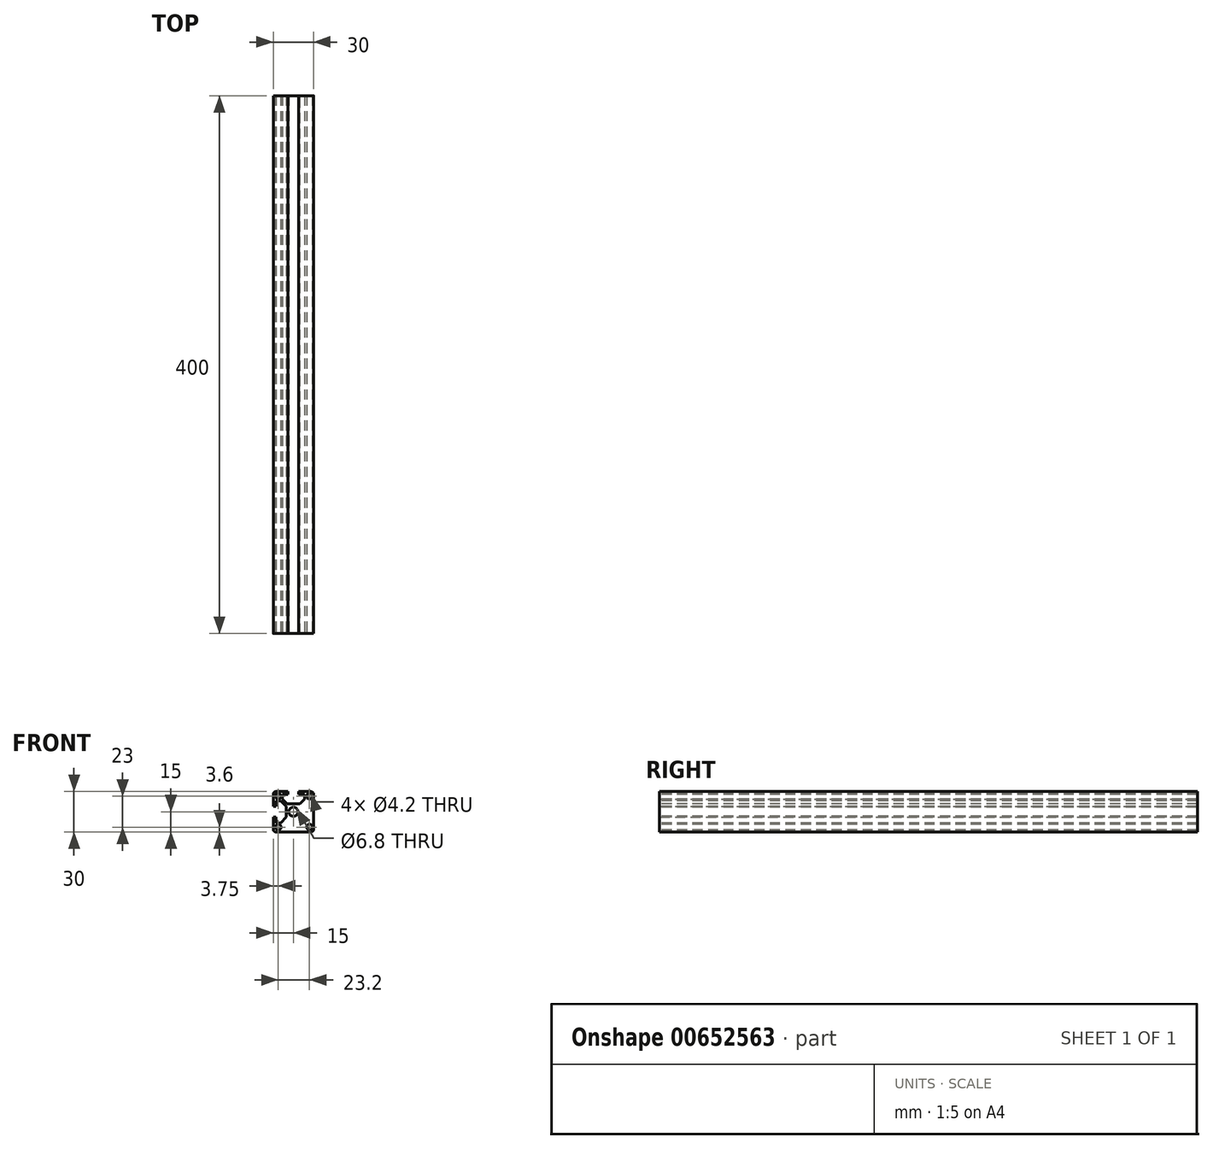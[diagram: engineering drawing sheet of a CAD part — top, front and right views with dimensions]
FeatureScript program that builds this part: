
annotation { "Feature Type Name" : "Feature", "Feature Type Description" : "" }
export const myFeature = defineFeature(function(context is Context, id is Id, definition is map)
    precondition{}
    {
        {
            var Q0;
            Q0=qCreatedBy(makeId("Front.planeOp"),FACE);
            var sketch = newSketch(context, id + "F0", { "sketchPlane" : qUnion([Q0])});
            skLineSegment(sketch, "E0.bottom", {"start": v(15, 15) * mm, "end": v(-15, 15) * mm});
            skLineSegment(sketch, "E0.top", {"start": v(15, -15) * mm, "end": v(-15, -15) * mm});
            skLineSegment(sketch, "E0.left", {"start": v(15, 15) * mm, "end": v(15, -15) * mm});
            skLineSegment(sketch, "E0.right", {"start": v(-15, 15) * mm, "end": v(-15, -15) * mm});
            skPoint(sketch, "E0.middle", {"position": v(0, 0) * mm});
            skSolve(sketch);
        }
        {
            var Q0;
            Q0=makeQuery(id+"F0.imprint","IMPRINT",FACE,{"disambiguationData":[TD([[makeQuery(id+"F0.imprint","IMPRINT",EDGE,{"derivedFrom":sQuery(id+"F0.wireOp",EDGE,"E0.bottom")}),1.0]])]});
            extrude(context, id + "F1", {"entities" : qUnion([Q0]), "depth" : 400 * mm, "offsetDistance" : 25 * mm});
        }
        {
            var Q0;
            Q0=makeQuery(id+"F1.opExtrude","CAP_FACE",FACE,{"disambiguationData":[OSD([sQuery(id+"F0.wireOp",EDGE,"E0.bottom"),sQuery(id+"F0.wireOp",EDGE,"E0.top"),sQuery(id+"F0.wireOp",EDGE,"E0.left"),sQuery(id+"F0.wireOp",EDGE,"E0.right")])],"isStart":false});
            var sketch = newSketch(context, id + "F2", { "sketchPlane" : qUnion([Q0])});
            skLineSegment(sketch, "E1.bottom", {"start": v(-4, 18.26) * mm, "end": v(4, 18.26) * mm});
            skLineSegment(sketch, "E1.top", {"start": v(-4, 13) * mm, "end": v(4, 13) * mm});
            skLineSegment(sketch, "E1.left", {"start": v(-4, 18.26) * mm, "end": v(-4, 13) * mm});
            skLineSegment(sketch, "E1.right", {"start": v(4, 18.26) * mm, "end": v(4, 13) * mm});
            skLineSegment(sketch, "E2.bottom", {"start": v(-8.25, 13) * mm, "end": v(8.25, 13) * mm});
            skLineSegment(sketch, "E2.top", {"start": v(-8.25, 6) * mm, "end": v(8.25, 6) * mm});
            skLineSegment(sketch, "E2.left", {"start": v(-8.25, 13) * mm, "end": v(-8.25, 6) * mm});
            skLineSegment(sketch, "E2.right", {"start": v(8.25, 13) * mm, "end": v(8.25, 6) * mm});
            skSolve(sketch);
        }
        {
            var Q0;
            Q0=makeQuery(id+"F2.imprint","IMPRINT",FACE,{"disambiguationData":[TD([[makeQuery(id+"F2.imprint","IMPRINT",EDGE,{"derivedFrom":sQuery(id+"F2.wireOp",EDGE,"E2.top")}),1.0]])]});
            var Q1;
            {var subQ0=sQuery(id+"F2.wireOp",EDGE,"E2.bottom");var subQ1=sQuery(id+"F2.wireOp",EDGE,"E1.left");var subQ2=makeQuery(id+"F2.imprint","INTERSECT",VERTEX,{"derivedFrom":[subQ1,subQ0]});Q1=makeQuery(id+"F2.imprint","IMPRINT",FACE,{"disambiguationData":[TD([[makeQuery(id+"F2.imprint","IMPRINT",EDGE,{"disambiguationData":[TD([[subQ2,1.0]])],"derivedFrom":subQ1}),1.0]])]});}
            var Q2;
            {var subQ0=sQuery(id+"F2.wireOp",EDGE,"E1.bottom");Q2=makeQuery(id+"F2.imprint","IMPRINT",FACE,{"disambiguationData":[TD([[makeQuery(id+"F2.imprint","IMPRINT",EDGE,{"derivedFrom":subQ0}),-1.0]])]});}
            extrude(context, id + "F3", {"entities" : qUnion([Q0, Q1, Q2]), "operationType" : NewBodyOperationType.REMOVE, "oppositeDirection" : true, "depth" : 400 * mm, "offsetDistance" : 25 * mm});
        }
        {
            var Q0;
            Q0=makeQuery(id+"F3.boolean.opBoolean","COPY",EDGE,{"derivedFrom":makeQuery(id+"F3.opExtrude","SWEPT_EDGE",EDGE,{"disambiguationData":[OSD([sQuery(id+"F2.wireOp",EDGE,"E2.top"),sQuery(id+"F2.wireOp",EDGE,"E2.left")])]})});
            var Q1;
            Q1=makeQuery(id+"F3.boolean.opBoolean","COPY",EDGE,{"derivedFrom":makeQuery(id+"F3.opExtrude","SWEPT_EDGE",EDGE,{"disambiguationData":[OSD([sQuery(id+"F2.wireOp",EDGE,"E2.top"),sQuery(id+"F2.wireOp",EDGE,"E2.right")])]})});
            chamfer(context, id + "F4", {"entities" : qUnion([Q0, Q1]), "width" : 3.5 * mm, "tangentPropagation" : true});
        }
        {
            var Q0;
            Q0=makeQuery(id+"F1.opExtrude","CAP_FACE",FACE,{"disambiguationData":[OSD([sQuery(id+"F0.wireOp",EDGE,"E0.bottom"),sQuery(id+"F0.wireOp",EDGE,"E0.top"),sQuery(id+"F0.wireOp",EDGE,"E0.left"),sQuery(id+"F0.wireOp",EDGE,"E0.right")])],"isStart":false});
            var sketch = newSketch(context, id + "F5", { "sketchPlane" : qUnion([Q0])});
            skLineSegment(sketch, "E3.bottom", {"start": v(-18.87, 4) * mm, "end": v(-13, 4) * mm});
            skLineSegment(sketch, "E3.top", {"start": v(-18.87, -4) * mm, "end": v(-13, -4) * mm});
            skLineSegment(sketch, "E3.left", {"start": v(-18.87, 4) * mm, "end": v(-18.87, -4) * mm});
            skLineSegment(sketch, "E4.bottom", {"start": v(-13, 8.25) * mm, "end": v(-9.5, 8.25) * mm});
            skLineSegment(sketch, "E4.top", {"start": v(-13, -8.25) * mm, "end": v(-9.5, -8.25) * mm});
            skLineSegment(sketch, "E4.left", {"start": v(-13, 8.25) * mm, "end": v(-13, 4) * mm});
            skLineSegment(sketch, "E4.right", {"start": v(-5.31, 4.06) * mm, "end": v(-5.31, -4.06) * mm});
            skLineSegment(sketch, "E5", {"start": v(-9.5, 8.25) * mm, "end": v(-5.31, 4.06) * mm});
            skLineSegment(sketch, "E6", {"start": v(-5.31, -4.06) * mm, "end": v(-9.5, -8.25) * mm});
            skLineSegment(sketch, "E7.trimOffspring", {"start": v(-13, -4) * mm, "end": v(-13, -8.25) * mm});
            skSolve(sketch);
        }
        {
            var Q0;
            {var subQ0=sQuery(id+"F5.wireOp",EDGE,"E3.left");Q0=makeQuery(id+"F5.imprint","IMPRINT",FACE,{"disambiguationData":[TD([[makeQuery(id+"F5.imprint","IMPRINT",EDGE,{"derivedFrom":subQ0}),1.0]])]});}
            var Q1;
            Q1=makeQuery(id+"F5.imprint","IMPRINT",FACE,{"disambiguationData":[TD([[makeQuery(id+"F5.imprint","IMPRINT",EDGE,{"derivedFrom":sQuery(id+"F5.wireOp",EDGE,"E4.bottom")}),-1.0]])]});
            extrude(context, id + "F6", {"entities" : qUnion([Q0, Q1]), "operationType" : NewBodyOperationType.REMOVE, "oppositeDirection" : true, "depth" : 400 * mm, "offsetDistance" : 25 * mm});
        }
        {
            var Q0;
            Q0=makeQuery(id+"F1.opExtrude","CAP_FACE",FACE,{"disambiguationData":[OSD([sQuery(id+"F0.wireOp",EDGE,"E0.bottom"),sQuery(id+"F0.wireOp",EDGE,"E0.top"),sQuery(id+"F0.wireOp",EDGE,"E0.left"),sQuery(id+"F0.wireOp",EDGE,"E0.right")])],"isStart":false});
            var sketch = newSketch(context, id + "F7", { "sketchPlane" : qUnion([Q0])});
            skCircle(sketch, "E8", {"center": v(0, 0) * mm, "radius": 3.4 * mm});
            skCircle(sketch, "E9", {"center": v(-11.25, 11.6) * mm, "radius": 2.1 * mm});
            skPoint(sketch, "E9.centerSnap0", {"position": v(-11.25, 8.25) * mm});
            skCircle(sketch, "E10", {"center": v(-11.25, -11.4) * mm, "radius": 2.1 * mm});
            skCircle(sketch, "E11", {"center": v(11.95, -11.4) * mm, "radius": 2.1 * mm});
            skCircle(sketch, "E12", {"center": v(11.95, 11.6) * mm, "radius": 2.1 * mm});
            skSolve(sketch);
        }
        {
            var Q0;
            Q0 = qSketchRegion(id + "F7", true);
            extrude(context, id + "F8", {"entities" : qUnion([Q0]), "operationType" : NewBodyOperationType.REMOVE, "oppositeDirection" : true, "depth" : 400 * mm, "offsetDistance" : 25 * mm});
        }
        {
            var Q0;
            Q0=makeQuery(id+"F1.opExtrude","SWEPT_EDGE",EDGE,{"disambiguationData":[OSD([sQuery(id+"F0.wireOp",EDGE,"E0.bottom"),sQuery(id+"F0.wireOp",EDGE,"E0.right")])]});
            var Q1;
            Q1=makeQuery(id+"F1.opExtrude","SWEPT_EDGE",EDGE,{"disambiguationData":[OSD([sQuery(id+"F0.wireOp",EDGE,"E0.top"),sQuery(id+"F0.wireOp",EDGE,"E0.right")])]});
            var Q2;
            Q2=makeQuery(id+"F1.opExtrude","SWEPT_EDGE",EDGE,{"disambiguationData":[OSD([sQuery(id+"F0.wireOp",EDGE,"E0.bottom"),sQuery(id+"F0.wireOp",EDGE,"E0.left")])]});
            var Q3;
            Q3=makeQuery(id+"F1.opExtrude","SWEPT_EDGE",EDGE,{"disambiguationData":[OSD([sQuery(id+"F0.wireOp",EDGE,"E0.top"),sQuery(id+"F0.wireOp",EDGE,"E0.left")])]});
            fillet(context, id + "F9", {"entities" : qUnion([Q0, Q1, Q2, Q3]), "radius" : 2 * mm, "tangentPropagation" : true, "allowEdgeOverflow" : false});
        }
    });
